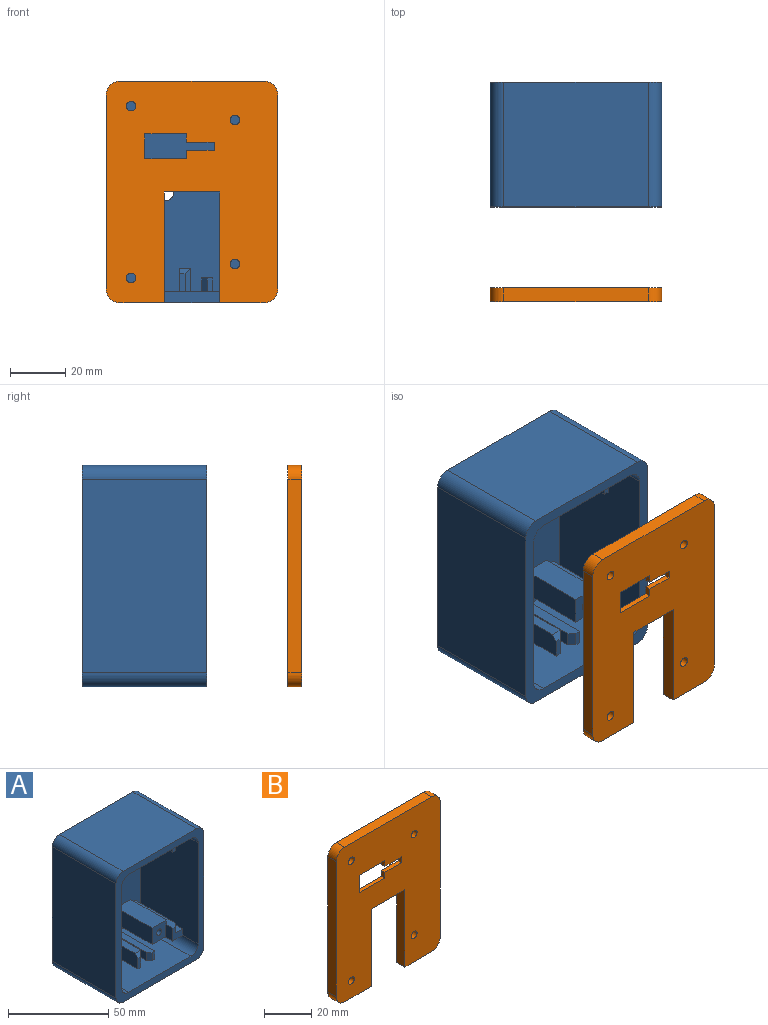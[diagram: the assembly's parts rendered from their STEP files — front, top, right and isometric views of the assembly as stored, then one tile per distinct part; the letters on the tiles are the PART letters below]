
ASSEMBLY  parts=2 mates=1
PART A: 81 faces, bbox 62x45x80 mm
  f0: plane 72x54mm, normal (0,-1,0), area 3152mm2, adj f1,f2,f3,f4,f5,f6,f13,f14
  f1: plane 30x8mm, normal (-1,0,0), area 46.3mm2, adj f0,f2,f15,f18,f64,f67
  f2: plane 30x4mm, normal (0,0,-1), area 105.5mm2, adj f0,f1,f16,f18,f30,f63,f67
  f3: plane 62x41mm, normal (1,0,0), area 2292mm2, adj f0,f7,f50,f51,f57,f58,f60,f62
  f4: plane 44x41mm, normal (0,0,-1), area 1443mm2, adj f0,f7,f19,f21,f22,f23,f24,f26
  f5: plane 62x41mm, normal (-1,0,0), area 2317mm2, adj f0,f7,f17,f18,f46,f47,f49,f52
  f6: plane 44x41mm, normal (0,0,1), area 1443mm2, adj f0,f7,f31,f32,f33,f35,f37,f38
  f7: plane 80x62mm, normal (0,-1,0), area 1072mm2, adj f3,f4,f5,f6,f8,f9,f10,f11
  f8: plane 70x45mm, normal (1,0,0), area 3150mm2, adj f7,f12,f53,f56
  f9: plane 52x45mm, normal (0,0,1), area 2340mm2, adj f7,f12,f53,f54
  f10: plane 70x45mm, normal (-1,0,0), area 3150mm2, adj f7,f12,f54,f55
  f11: plane 52x45mm, normal (0,0,-1), area 2340mm2, adj f7,f12,f55,f56
  f12: plane 80x62mm, normal (0,1,0), area 4801.5mm2, adj f8,f9,f10,f11,f13,f14,f53,f54
  f13: cylinder r=3.25mm len=6.5mm, axis (0,1,0), area 81.7mm2, adj f0,f12
  f14: cylinder r=5.75mm len=11.5mm, axis (0,1,0), area 144.5mm2, adj f0,f12
  f15: plane 30x6.99mm, normal (0,0,1), area 209.8mm2, adj f0,f1,f18,f49
  f16: plane 28x4mm, normal (1,0,0), area 112mm2, adj f0,f2,f17,f30
  f17: plane 30x5mm, normal (0,0,-1), area 92mm2, adj f0,f5,f16,f18,f30
  f18: plane 8x7mm, normal (0,-1,0), area 36mm2, adj f1,f2,f5,f15,f17,f30,f49
  f19: plane 28x5mm, normal (-1,0,0), area 140mm2, adj f0,f4,f20,f29
  f20: plane 30x4mm, normal (0,0,-1), area 118mm2, adj f0,f19,f21,f22,f29
  f21: plane 30x5mm, normal (1,0,0), area 150mm2, adj f0,f4,f20,f22
  f22: plane 5x2mm, normal (0,-1,0), area 10mm2, adj f4,f20,f21,f29
  f23: plane 28x8.5mm, normal (1,0,0), area 238mm2, adj f0,f4,f25,f27
  f24: plane 30x8.5mm, normal (-1,0,0), area 253mm2, adj f0,f4,f25,f26,f28
  f25: plane 28x4mm, normal (0,0,-1), area 112mm2, adj f0,f23,f24,f28
  f26: plane 6.5x2mm, normal (0,-1,0), area 13mm2, adj f4,f24,f27,f28
  f27: plane 8.5x2mm, normal (0.71,-0.71,0), area 21.2mm2, adj f4,f23,f26,f28
  f28: plane 4x2mm, normal (0,-0.71,-0.71), area 8.5mm2, adj f24,f25,f26,f27
  f29: plane 5x2mm, normal (-0.71,-0.71,0), area 14.1mm2, adj f4,f19,f20,f22
  f30: plane 4x2mm, normal (0.71,-0.71,0), area 11.3mm2, adj f2,f16,f17,f18
  f31: plane 5x2mm, normal (-0.71,-0.71,0), area 14.1mm2, adj f6,f32,f34,f35
  f32: plane 5x2mm, normal (0,-1,0), area 10mm2, adj f6,f31,f33,f34
  f33: plane 30x5mm, normal (1,0,0), area 150mm2, adj f0,f6,f32,f34
  f34: plane 30x4mm, normal (0,0,1), area 118mm2, adj f0,f31,f32,f33,f35
  f35: plane 28x5mm, normal (-1,0,0), area 140mm2, adj f0,f6,f31,f34
  f36: plane 4x2mm, normal (0,-0.71,0.71), area 8.5mm2, adj f37,f38,f39,f40
  f37: plane 8.5x2mm, normal (0.71,-0.71,0), area 21.2mm2, adj f6,f36,f38,f41
  f38: plane 6.5x2mm, normal (0,-1,0), area 13mm2, adj f6,f36,f37,f40
  f39: plane 28x4mm, normal (0,0,1), area 112mm2, adj f0,f36,f40,f41
  f40: plane 30x8.5mm, normal (-1,0,0), area 253mm2, adj f0,f6,f36,f38,f39
  f41: plane 28x8.5mm, normal (1,0,0), area 238mm2, adj f0,f6,f37,f39
  f42: plane 30x6.99mm, normal (0,0,-1), area 209.8mm2, adj f0,f43,f47,f52
  f43: plane 30x8mm, normal (-1,0,0), area 46.3mm2, adj f0,f42,f44,f47,f69,f72
  f44: plane 30x4mm, normal (0,0,1), area 105.5mm2, adj f0,f43,f45,f47,f48,f70,f72
  f45: plane 28x4mm, normal (1,0,0), area 112mm2, adj f0,f44,f46,f48
  f46: plane 30x5mm, normal (0,0,1), area 92mm2, adj f0,f5,f45,f47,f48
  f47: plane 8x7mm, normal (0,-1,0), area 36mm2, adj f5,f42,f43,f44,f46,f48,f52
  f48: plane 4x2mm, normal (0.71,-0.71,0), area 11.3mm2, adj f44,f45,f46,f47
  f49: cylinder r=5mm len=41mm, axis (0,-1,0), area 314.5mm2, adj f0,f4,f5,f7,f15,f18
  f50: cylinder r=5mm len=16mm, axis (0,1,0), area 125.7mm2, adj f3,f4,f7,f57
  f51: cylinder r=5mm len=16mm, axis (0,-1,0), area 125.7mm2, adj f3,f6,f7,f60
  f52: cylinder r=5mm len=41mm, axis (0,1,0), area 314.5mm2, adj f0,f5,f6,f7,f42,f47
  f53: cylinder r=5mm len=45mm, axis (0,-1,0), area 353.4mm2, adj f7,f8,f9,f12
  f54: cylinder r=5mm len=45mm, axis (0,1,0), area 353.4mm2, adj f7,f9,f10,f12
  f55: cylinder r=5mm len=45mm, axis (0,-1,0), area 353.4mm2, adj f7,f10,f11,f12
  f56: cylinder r=5mm len=45mm, axis (0,1,0), area 353.4mm2, adj f7,f8,f11,f12
  f57: plane 10x10mm, normal (0,-1,0), area 85mm2, adj f3,f4,f50,f58,f59,f79
  f58: plane 25x10mm, normal (0,0,-1), area 250mm2, adj f0,f3,f57,f59
  f59: plane 25x10mm, normal (1,0,0), area 250mm2, adj f0,f4,f57,f58
  f60: plane 10x10mm, normal (0,-1,0), area 85mm2, adj f3,f6,f51,f61,f62,f77
  f61: plane 25x10mm, normal (1,0,0), area 250mm2, adj f0,f6,f60,f62
  f62: plane 25x10mm, normal (0,0,1), area 250mm2, adj f0,f3,f60,f61
  f63: plane 25x2.25mm, normal (1,0,0), area 56.2mm2, adj f0,f2,f66,f67
  f64: plane 25x9.5mm, normal (0,0,1), area 237.5mm2, adj f0,f1,f65,f67
  f65: plane 25x10mm, normal (-1,0,0), area 250mm2, adj f0,f64,f66,f67
  f66: plane 25x10mm, normal (0,0,-1), area 250mm2, adj f0,f63,f65,f67
  f67: plane 10x10mm, normal (0,-1,0), area 86.5mm2, adj f1,f2,f63,f64,f65,f66,f75
  f68: plane 25x10mm, normal (-1,0,0), area 250mm2, adj f0,f69,f71,f72
  f69: plane 25x9.5mm, normal (0,0,-1), area 237.5mm2, adj f0,f43,f68,f72
  f70: plane 25x2.25mm, normal (1,0,0), area 56.2mm2, adj f0,f44,f71,f72
  f71: plane 25x10mm, normal (0,0,1), area 250mm2, adj f0,f68,f70,f72
  f72: plane 10x10mm, normal (0,-1,0), area 86.5mm2, adj f43,f44,f68,f69,f70,f71,f73
  f73: cylinder r=1.75mm len=15mm, axis (0,-1,0), area 164.9mm2, adj f72,f74
  f74: plane 3.5x3.5mm, normal (0,-1,0), area 9.6mm2, adj f73
  f75: cylinder r=1.75mm len=15mm, axis (0,-1,0), area 164.9mm2, adj f67,f76
  f76: plane 3.5x3.5mm, normal (0,-1,0), area 9.6mm2, adj f75
  f77: cylinder r=1.75mm len=15mm, axis (0,-1,0), area 164.9mm2, adj f60,f78
  f78: plane 3.5x3.5mm, normal (0,-1,0), area 9.6mm2, adj f77
  f79: cylinder r=1.75mm len=15mm, axis (0,-1,0), area 164.9mm2, adj f57,f80
  f80: plane 3.5x3.5mm, normal (0,-1,0), area 9.6mm2, adj f79
PART B: 31 faces, bbox 62x5x80 mm
  f0: plane 80x62mm, normal (0,1,0), area 3500.1mm2, adj f10,f11,f12,f13,f14,f15,f16,f17
  f1: plane 10x2mm, normal (0,0,-1), area 20mm2, adj f2,f8,f9,f30
  f2: plane 3x2mm, normal (-1,0,0), area 6mm2, adj f1,f3,f9,f30
  f3: plane 15x2mm, normal (0,0,-1), area 30mm2, adj f2,f4,f9,f30
  f4: plane 9x2mm, normal (1,0,0), area 18mm2, adj f3,f5,f9,f30
  f5: plane 15x2mm, normal (0,0,1), area 30mm2, adj f4,f6,f9,f30
  f6: plane 3x2mm, normal (-1,0,0), area 6mm2, adj f5,f7,f9,f30
  f7: plane 10x2mm, normal (0,0,1), area 20mm2, adj f6,f8,f9,f30
  f8: plane 3x2mm, normal (-1,0,0), area 6mm2, adj f1,f7,f9,f30
  f9: plane 80x62mm, normal (0,-1,0), area 3935.1mm2, adj f1,f2,f3,f4,f5,f6,f7,f8
  f10: plane 16x5mm, normal (0,0,-1), area 80mm2, adj f0,f9,f18,f24
  f11: plane 70x5mm, normal (1,0,0), area 350mm2, adj f0,f9,f22,f25
  f12: plane 52x5mm, normal (0,0,1), area 260mm2, adj f0,f9,f22,f23
  f13: plane 70x5mm, normal (-1,0,0), area 350mm2, adj f0,f9,f23,f24
  f14: plane 16x5mm, normal (0,0,-1), area 80mm2, adj f0,f9,f19,f25
  f15: cylinder r=1.75mm len=5mm, axis (0,-1,0), area 55mm2, adj f0,f9
  f16: cylinder r=1.75mm len=5mm, axis (0,-1,0), area 55mm2, adj f0,f9
  f17: cylinder r=1.75mm len=5mm, axis (0,-1,0), area 55mm2, adj f0,f9
  f18: plane 40x5mm, normal (1,0,0), area 200mm2, adj f0,f9,f10,f20
  f19: plane 40x5mm, normal (-1,0,0), area 200mm2, adj f0,f9,f14,f20
  f20: plane 20x5mm, normal (0,0,-1), area 100mm2, adj f0,f9,f18,f19
  f21: cylinder r=1.75mm len=5mm, axis (0,-1,0), area 55mm2, adj f0,f9
  f22: cylinder r=5mm len=5mm, axis (0,-1,0), area 39.3mm2, adj f0,f9,f11,f12
  f23: cylinder r=5mm len=5mm, axis (0,1,0), area 39.3mm2, adj f0,f9,f12,f13
  f24: cylinder r=5mm len=5mm, axis (0,-1,0), area 39.3mm2, adj f0,f9,f10,f13
  f25: cylinder r=5mm len=5mm, axis (0,1,0), area 39.3mm2, adj f0,f9,f11,f14
  f26: plane 30x3mm, normal (0,0,-1), area 90mm2, adj f0,f27,f29,f30
  f27: plane 20x3mm, normal (-1,0,0), area 60mm2, adj f0,f26,f28,f30
  f28: plane 30x3mm, normal (0,0,1), area 90mm2, adj f0,f27,f29,f30
  f29: plane 20x3mm, normal (1,0,0), area 60mm2, adj f0,f26,f28,f30
  f30: plane 30x20mm, normal (0,1,0), area 435mm2, adj f1,f2,f3,f4,f5,f6,f7,f8
PLACE A t=(73.72,59.53,30.8)mm
PLACE B t=(73.72,-14.68,30.8)mm
MATE cylindrical B.f21 <-> A.f50  axis (0,-1,0) through (51.72,-17.18,61.8)mm
